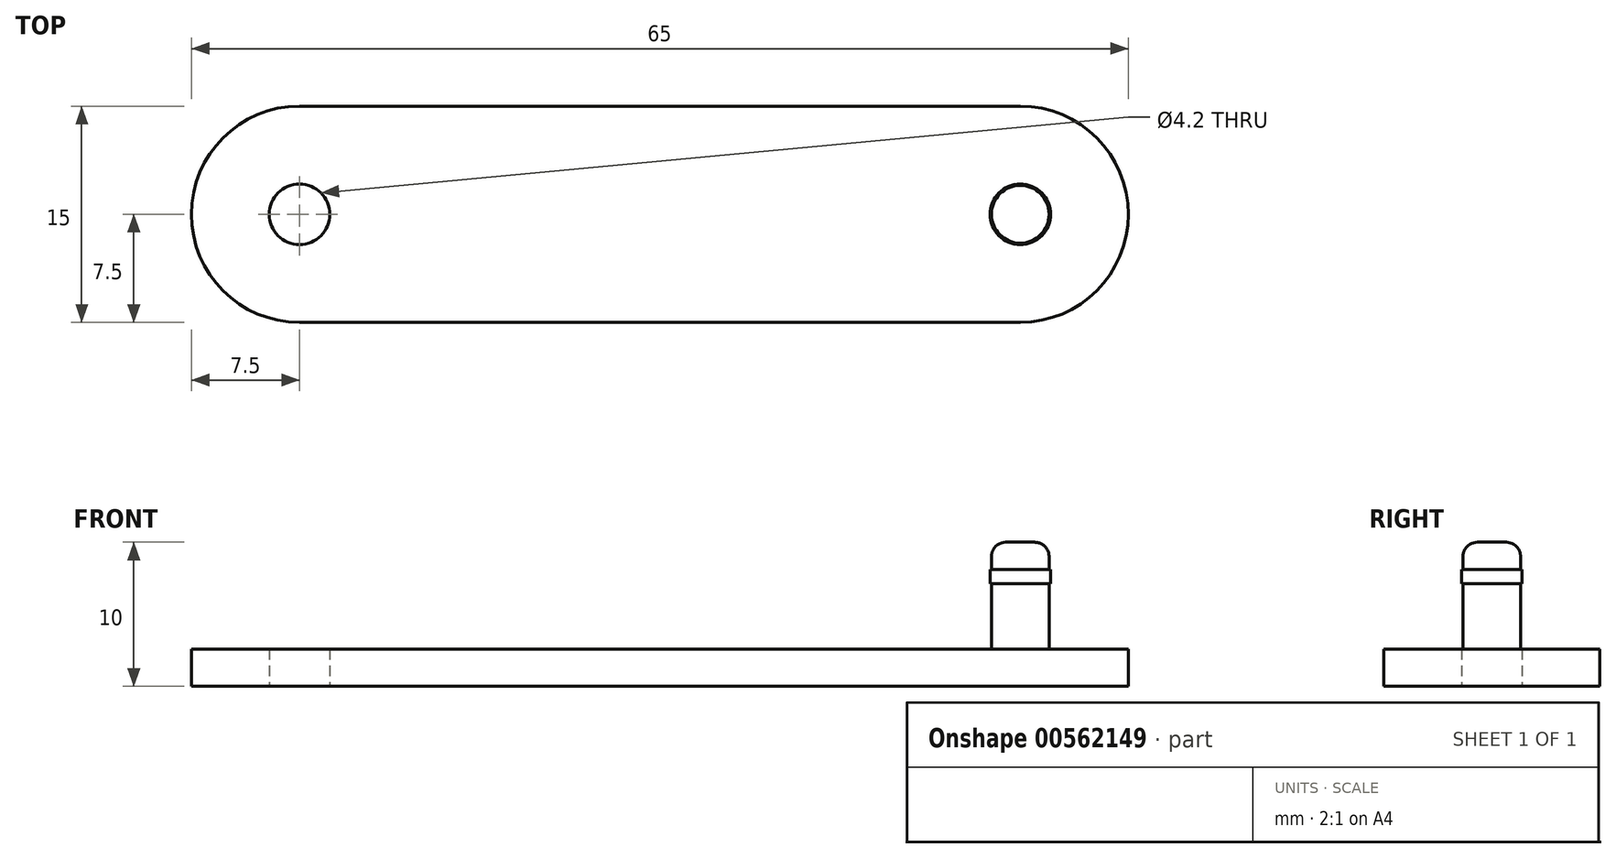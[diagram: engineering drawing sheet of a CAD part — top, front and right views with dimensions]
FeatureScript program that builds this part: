
annotation { "Feature Type Name" : "Feature", "Feature Type Description" : "" }
export const myFeature = defineFeature(function(context is Context, id is Id, definition is map)
    precondition{}
    {
        {
            var Q0;
            Q0=qCreatedBy(makeId("Top.planeOp"),FACE);
            var sketch = newSketch(context, id + "F0", { "sketchPlane" : qUnion([Q0])});
            skLineSegment(sketch, "E0", {"start": v(0, 0) * mm, "end": v(-25, 0) * mm, "construction": true});
            skLineSegment(sketch, "E1", {"start": v(0, 0) * mm, "end": v(25, 0) * mm, "construction": true});
            skArc(sketch, "E2", {"start": v(-25, 7.5) * mm, "mid": v(-32.5, 0) * mm, "end": v(-25, -7.5) * mm});
            skArc(sketch, "E3", {"start": v(25, -7.5) * mm, "mid": v(32.5, 0) * mm, "end": v(25, 7.5) * mm});
            skCircle(sketch, "E4", {"center": v(-25, 0) * mm, "radius": 2.1 * mm});
            skLineSegment(sketch, "E5", {"start": v(-25, 0) * mm, "end": v(-25, 7.5) * mm, "construction": true});
            skLineSegment(sketch, "E6", {"start": v(-25, 0) * mm, "end": v(-25, -7.5) * mm, "construction": true});
            skLineSegment(sketch, "E7", {"start": v(-25, 7.5) * mm, "end": v(25, 7.5) * mm});
            skLineSegment(sketch, "E8", {"start": v(-25, -7.5) * mm, "end": v(25, -7.5) * mm});
            skCircle(sketch, "E9", {"center": v(25, 0) * mm, "radius": 2 * mm});
            skSolve(sketch);
        }
        {
            var Q0;
            Q0=makeQuery(id+"F0.imprint","IMPRINT",FACE,{"disambiguationData":[TD([[makeQuery(id+"F0.imprint","IMPRINT",EDGE,{"derivedFrom":sQuery(id+"F0.wireOp",EDGE,"E9")}),1.0]])]});
            extrude(context, id + "F1", {"entities" : qUnion([Q0]), "depth" : 10 * mm, "offsetDistance" : 25 * mm});
        }
        {
            var Q0;
            Q0=makeQuery(id+"F0.imprint","IMPRINT",FACE,{"disambiguationData":[TD([[makeQuery(id+"F0.imprint","IMPRINT",EDGE,{"derivedFrom":sQuery(id+"F0.wireOp",EDGE,"E2")}),1.0]])]});
            extrude(context, id + "F2", {"entities" : qUnion([Q0]), "operationType" : NewBodyOperationType.ADD, "depth" : 2.6 * mm, "offsetDistance" : 25 * mm});
        }
        {
            var Q0;
            Q0=qCreatedBy(makeId("Right.planeOp"),FACE);
            cPlane(context, id + "F3", {"entities" : qUnion([Q0]), "cplaneType" : CPlaneType.OFFSET, "offset" : 25 * mm, "width" : 150 * mm, "height" : 150 * mm});
        }
        {
            var Q0;
            Q0=makeQuery(id+"F1.opExtrude","CAP_EDGE",EDGE,{"disambiguationData":[OSD([sQuery(id+"F0.wireOp",EDGE,"E9")])],"isStart":false});
            fillet(context, id + "F4", {"entities" : qUnion([Q0]), "radius" : 1 * mm, "tangentPropagation" : true, "allowEdgeOverflow" : false});
        }
        {
            var Q0;
            Q0=qCreatedBy(id+"F3.planeOp",FACE);
            var sketch = newSketch(context, id + "F5", { "sketchPlane" : qUnion([Q0])});
            skLineSegment(sketch, "E10.0", {"start": v(2, 9) * mm, "end": v(-2, 9) * mm, "construction": true});
            skLineSegment(sketch, "E11", {"start": v(-2, 2.6) * mm, "end": v(-2, 9) * mm, "construction": true});
            skLineSegment(sketch, "E12", {"start": v(2, 9) * mm, "end": v(2, 2.6) * mm, "construction": true});
            skLineSegment(sketch, "E13", {"start": v(0, 8.12) * mm, "end": v(-2.1, 8.12) * mm});
            skPoint(sketch, "E13.startSnap0", {"position": v(0, 9) * mm});
            skLineSegment(sketch, "E14", {"start": v(-2.1, 8.12) * mm, "end": v(-2.1, 7.12) * mm});
            skLineSegment(sketch, "E15", {"start": v(-2.1, 7.12) * mm, "end": v(2.1, 7.12) * mm});
            skLineSegment(sketch, "E16", {"start": v(2.1, 7.12) * mm, "end": v(2.1, 8.12) * mm});
            skLineSegment(sketch, "E17", {"start": v(2.1, 8.12) * mm, "end": v(0, 8.12) * mm});
            skLineSegment(sketch, "E18", {"start": v(0, 8.12) * mm, "end": v(0, 7.12) * mm});
            skSolve(sketch);
        }
        {
            var Q0;
            Q0=makeQuery(id+"F5.imprint","IMPRINT",FACE,{"disambiguationData":[TD([[makeQuery(id+"F5.imprint","IMPRINT",EDGE,{"derivedFrom":sQuery(id+"F5.wireOp",EDGE,"E13")}),1.0]])]});
            var Q1;
            Q1=sQuery(id+"F5.wireOp",EDGE,"E18");
            revolve(context, id + "F6", {"operationType" : NewBodyOperationType.ADD, "entities" : qUnion([Q0]), "axis" : qUnion([Q1]), "revolveType" : RevolveType.FULL});
        }
    });
